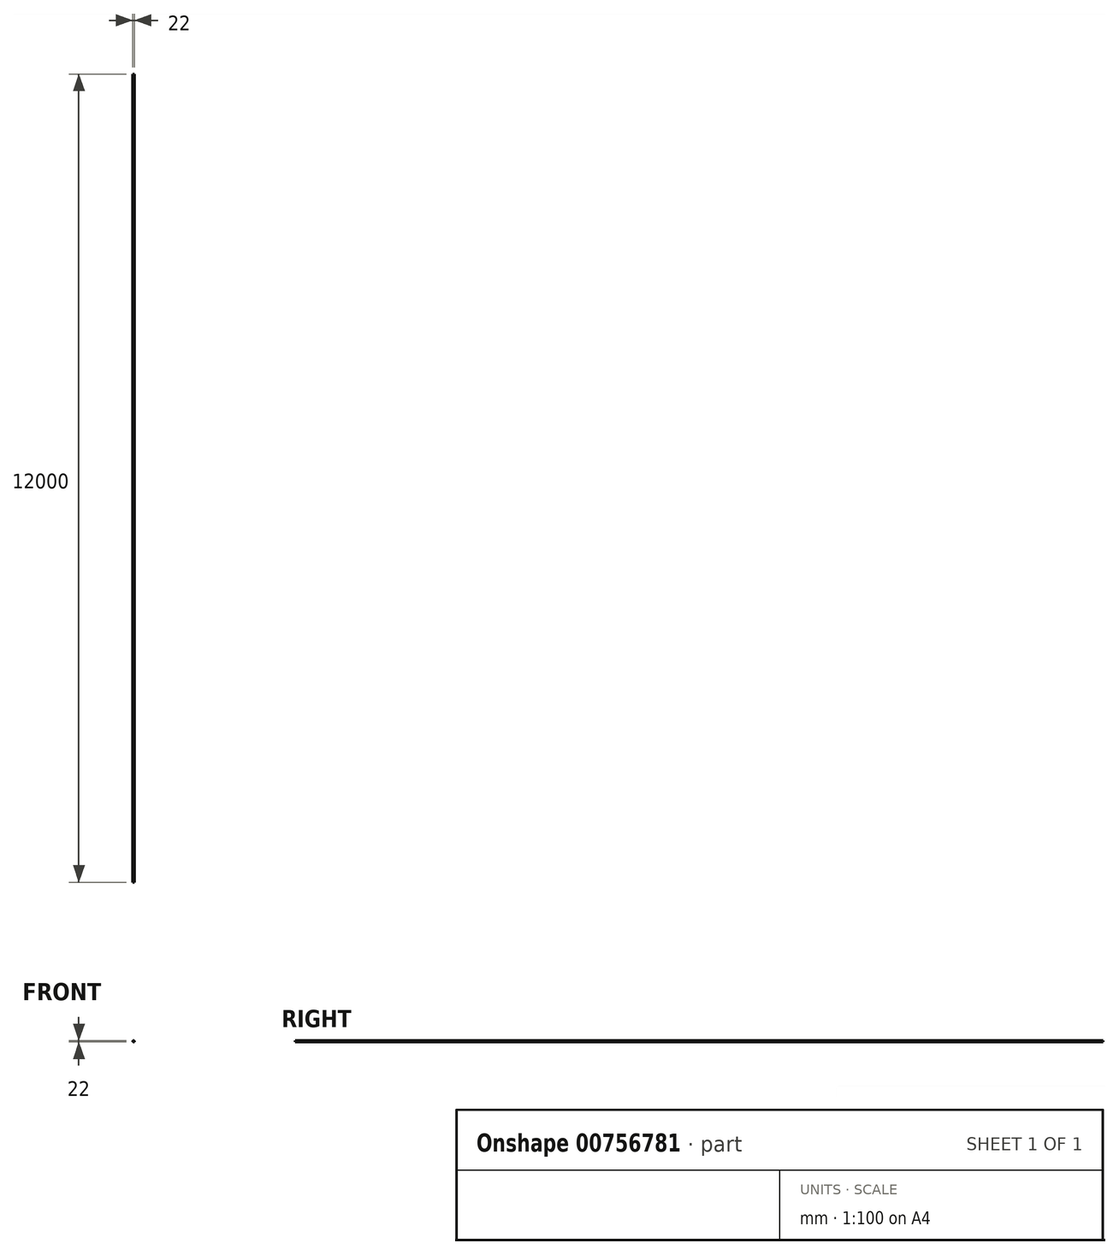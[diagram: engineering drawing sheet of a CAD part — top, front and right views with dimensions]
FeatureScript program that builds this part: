
annotation { "Feature Type Name" : "Feature", "Feature Type Description" : "" }
export const myFeature = defineFeature(function(context is Context, id is Id, definition is map)
    precondition{}
    {
        {
            var Q0;
            Q0=qCreatedBy(makeId("Front.planeOp"),FACE);
            var sketch = newSketch(context, id + "F0", { "sketchPlane" : qUnion([Q0])});
            skCircle(sketch, "E0", {"center": v(0, 0) * mm, "radius": 11 * mm});
            skSolve(sketch);
        }
        {
            var Q0;
            Q0=makeQuery(id+"F0.imprint","IMPRINT",FACE,{"disambiguationData":[TD([[makeQuery(id+"F0.imprint","IMPRINT",EDGE,{"derivedFrom":sQuery(id+"F0.wireOp",EDGE,"E0")}),1.0]])]});
            extrude(context, id + "F1", {"entities" : qUnion([Q0]), "endBound" : BoundingType.SYMMETRIC, "depth" : 12000 * mm, "offsetDistance" : 25 * mm});
        }
    });
